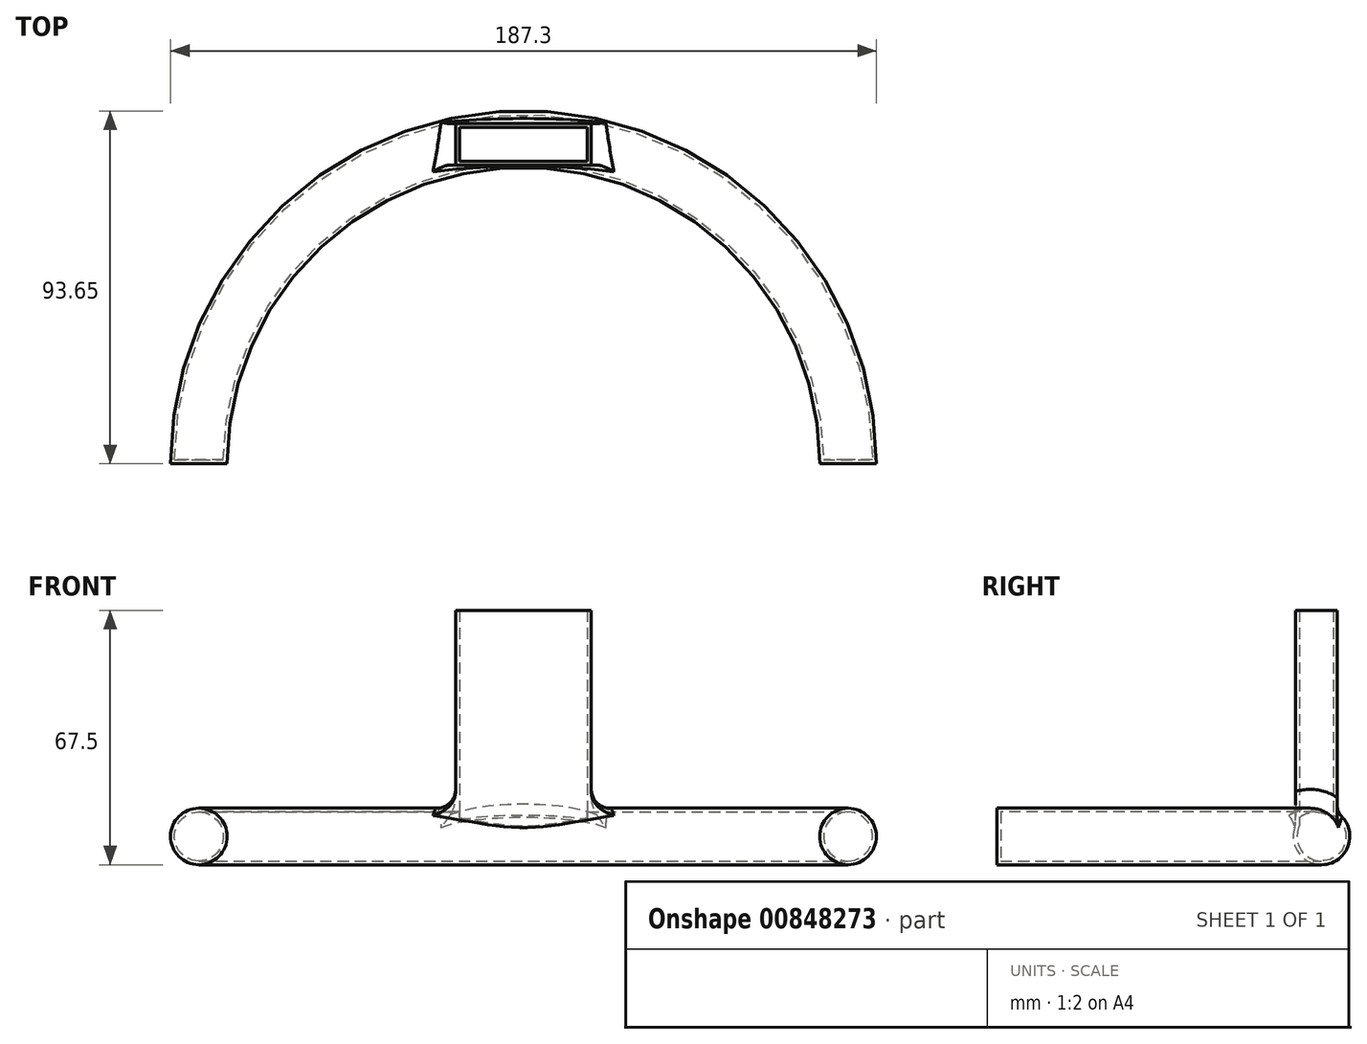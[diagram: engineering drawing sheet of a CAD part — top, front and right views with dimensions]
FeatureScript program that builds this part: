
annotation { "Feature Type Name" : "Feature", "Feature Type Description" : "" }
export const myFeature = defineFeature(function(context is Context, id is Id, definition is map)
    precondition{}
    {
        {
            var Q0;
            Q0=qCreatedBy(makeId("Top.planeOp"),FACE);
            var sketch = newSketch(context, id + "F0", { "sketchPlane" : qUnion([Q0])});
            skArc(sketch, "E0", {"start": v(75, 0) * mm, "mid": v(0, 75) * mm, "end": v(-75, 0) * mm});
            skPoint(sketch, "E1.orphan", {"position": v(-86.15, 0) * mm});
            skSolve(sketch);
        }
        {
            var Q0;
            Q0=qCreatedBy(makeId("Front.planeOp"),FACE);
            var sketch = newSketch(context, id + "F1", { "sketchPlane" : qUnion([Q0])});
            skCircle(sketch, "E2", {"center": v(-86.15, 0) * mm, "radius": 7.5 * mm});
            skSolve(sketch);
        }
        {
            var Q0;
            Q0=makeQuery(id+"F1.imprint","IMPRINT",FACE,{"disambiguationData":[TD([[makeQuery(id+"F1.imprint","IMPRINT",EDGE,{"derivedFrom":sQuery(id+"F1.wireOp",EDGE,"E2")}),1.0]])]});
            var Q1;
            Q1=sQuery(id+"F0.wireOp",EDGE,"E0");
            sweep(context, id + "F2", {"profiles" : qUnion([Q0]), "path" : qUnion([Q1])});
        }
        {
            var Q0;
            Q0=qCreatedBy(makeId("Top.planeOp"),FACE);
            var sketch = newSketch(context, id + "F3", { "sketchPlane" : qUnion([Q0])});
            skLineSegment(sketch, "E3.bottom", {"start": v(18, 90.28) * mm, "end": v(-18, 90.28) * mm});
            skLineSegment(sketch, "E3.top", {"start": v(18, 79.28) * mm, "end": v(-18, 79.28) * mm});
            skLineSegment(sketch, "E3.left", {"start": v(18, 90.28) * mm, "end": v(18, 79.28) * mm});
            skLineSegment(sketch, "E3.right", {"start": v(-18, 90.28) * mm, "end": v(-18, 79.28) * mm});
            skSolve(sketch);
        }
        {
            var Q0;
            Q0 = qSketchRegion(id + "F3", true);
            extrude(context, id + "F4", {"entities" : qUnion([Q0]), "operationType" : NewBodyOperationType.ADD, "depth" : 60 * mm, "offsetDistance" : 25 * mm});
        }
        {
            var Q0;
            Q0=makeQuery(id+"F4.opExtrude","CAP_FACE",FACE,{"disambiguationData":[OSD([sQuery(id+"F3.wireOp",EDGE,"E3.bottom"),sQuery(id+"F3.wireOp",EDGE,"E3.top"),sQuery(id+"F3.wireOp",EDGE,"E3.left"),sQuery(id+"F3.wireOp",EDGE,"E3.right")])],"isStart":false});
            shell(context, id + "F5", {"entities" : qUnion([Q0]), "thickness" : 1 * mm});
        }
        {
            var Q0;
            Q0=makeQuery(id+"F4.boolean.opBoolean","INTERSECT",EDGE,{"derivedFrom":[makeQuery(id+"F2.opSweep","SWEPT_FACE",FACE,{"disambiguationData":[OSD([sQuery(id+"F0.wireOp",EDGE,"E0"),sQuery(id+"F1.wireOp",EDGE,"E2")])]}),makeQuery(id+"F4.opExtrude","SWEPT_FACE",FACE,{"disambiguationData":[OSD([sQuery(id+"F3.wireOp",EDGE,"E3.bottom")])]})]});
            var Q1;
            Q1=makeQuery(id+"F4.boolean.opBoolean","INTERSECT",EDGE,{"derivedFrom":[makeQuery(id+"F2.opSweep","SWEPT_FACE",FACE,{"disambiguationData":[OSD([sQuery(id+"F0.wireOp",EDGE,"E0"),sQuery(id+"F1.wireOp",EDGE,"E2")])]}),makeQuery(id+"F4.opExtrude","SWEPT_FACE",FACE,{"disambiguationData":[OSD([sQuery(id+"F3.wireOp",EDGE,"E3.right")])]})]});
            var Q2;
            Q2=makeQuery(id+"F4.boolean.opBoolean","INTERSECT",EDGE,{"derivedFrom":[makeQuery(id+"F2.opSweep","SWEPT_FACE",FACE,{"disambiguationData":[OSD([sQuery(id+"F0.wireOp",EDGE,"E0"),sQuery(id+"F1.wireOp",EDGE,"E2")])]}),makeQuery(id+"F4.opExtrude","SWEPT_FACE",FACE,{"disambiguationData":[OSD([sQuery(id+"F3.wireOp",EDGE,"E3.top")])]})]});
            var Q3;
            Q3=makeQuery(id+"F4.boolean.opBoolean","INTERSECT",EDGE,{"derivedFrom":[makeQuery(id+"F2.opSweep","SWEPT_FACE",FACE,{"disambiguationData":[OSD([sQuery(id+"F0.wireOp",EDGE,"E0"),sQuery(id+"F1.wireOp",EDGE,"E2")])]}),makeQuery(id+"F4.opExtrude","SWEPT_FACE",FACE,{"disambiguationData":[OSD([sQuery(id+"F3.wireOp",EDGE,"E3.left")])]})]});
            fillet(context, id + "F6", {"entities" : qUnion([Q0, Q1, Q2, Q3]), "radius" : 5 * mm, "tangentPropagation" : true, "allowEdgeOverflow" : false});
        }
    });
